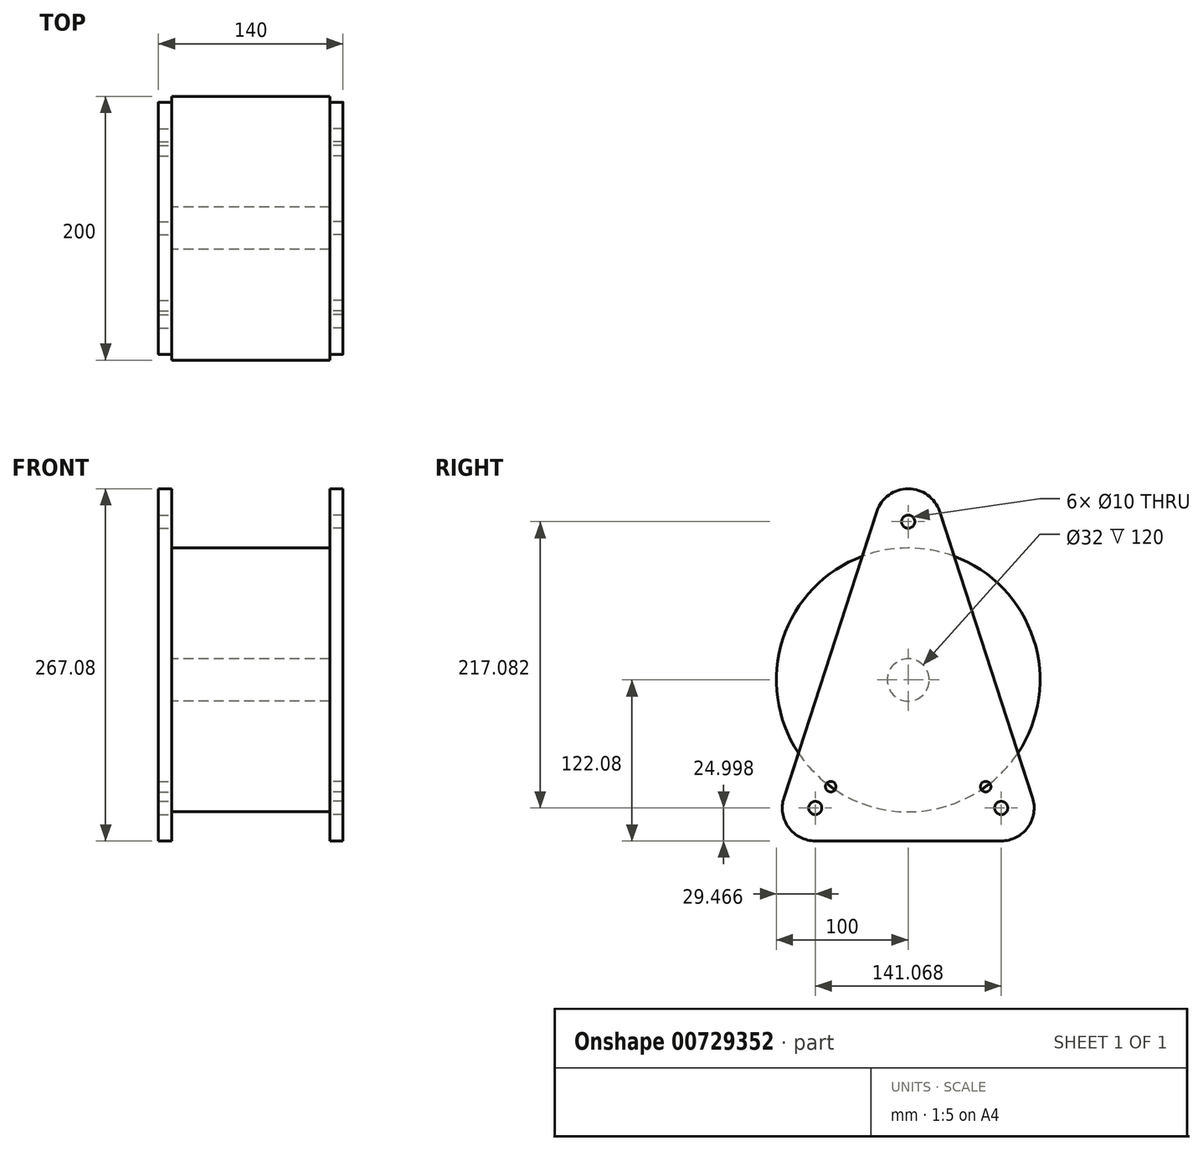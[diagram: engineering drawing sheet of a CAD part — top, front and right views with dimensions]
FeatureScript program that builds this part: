
annotation { "Feature Type Name" : "Feature", "Feature Type Description" : "" }
export const myFeature = defineFeature(function(context is Context, id is Id, definition is map)
    precondition{}
    {
        {
            var Q0;
            Q0=qCreatedBy(makeId("Right.planeOp"),FACE);
            var sketch = newSketch(context, id + "F0", { "sketchPlane" : qUnion([Q0])});
            skCircle(sketch, "E0", {"center": v(0, 0) * mm, "radius": 100 * mm});
            skCircle(sketch, "E1", {"center": v(0, 0) * mm, "radius": 16 * mm});
            skSolve(sketch);
        }
        {
            var Q0;
            Q0=makeQuery(id+"F0.imprint","IMPRINT",FACE,{"disambiguationData":[TD([[makeQuery(id+"F0.imprint","IMPRINT",EDGE,{"derivedFrom":sQuery(id+"F0.wireOp",EDGE,"E0")}),1.0]])]});
            extrude(context, id + "F1", {"entities" : qUnion([Q0]), "depth" : 60 * mm, "offsetDistance" : 25 * mm});
        }
        {
            var Q0;
            Q0=makeQuery(id+"F1.opExtrude","CAP_FACE",FACE,{"disambiguationData":[OSD([sQuery(id+"F0.wireOp",EDGE,"E0"),sQuery(id+"F0.wireOp",EDGE,"E1")])],"isStart":false});
            var sketch = newSketch(context, id + "F2", { "sketchPlane" : qUnion([Q0])});
            skLineSegment(sketch, "E2", {"start": v(0, 0) * mm, "end": v(0, 120) * mm, "construction": true});
            skLineSegment(sketch, "E3.2.0", {"start": v(0, 0) * mm, "end": v(-70.53, -97.08) * mm, "construction": true});
            skLineSegment(sketch, "E3.3.0", {"start": v(0, 0) * mm, "end": v(70.53, -97.08) * mm, "construction": true});
            skPoint(sketch, "E3.center", {"position": v(0, 0) * mm});
            skArc(sketch, "E4", {"start": v(-94.31, -89.36) * mm, "mid": v(-90.76, -111.78) * mm, "end": v(-70.53, -122.08) * mm});
            skArc(sketch, "E5", {"start": v(70.53, -122.08) * mm, "mid": v(90.76, -111.78) * mm, "end": v(94.31, -89.36) * mm});
            skLineSegment(sketch, "E6", {"start": v(0, 120) * mm, "end": v(-70.53, -97.08) * mm, "construction": true});
            skLineSegment(sketch, "E7", {"start": v(70.53, -97.08) * mm, "end": v(0, 120) * mm, "construction": true});
            skLineSegment(sketch, "E8", {"start": v(70.53, -97.08) * mm, "end": v(-70.53, -97.08) * mm, "construction": true});
            skLineSegment(sketch, "E9", {"start": v(-23.78, 127.73) * mm, "end": v(-94.31, -89.36) * mm});
            skLineSegment(sketch, "E10", {"start": v(23.78, 127.73) * mm, "end": v(94.31, -89.36) * mm});
            skLineSegment(sketch, "E11", {"start": v(-70.53, -122.08) * mm, "end": v(70.53, -122.08) * mm});
            skPoint(sketch, "E12", {"position": v(-94.31, -89.36) * mm});
            skPoint(sketch, "E13", {"position": v(-70.53, -122.08) * mm});
            skPoint(sketch, "E14", {"position": v(70.53, -122.08) * mm});
            skPoint(sketch, "E15", {"position": v(94.31, -89.36) * mm});
            skPoint(sketch, "E16", {"position": v(23.78, 127.73) * mm});
            skPoint(sketch, "E17", {"position": v(-23.78, 127.73) * mm});
            skArc(sketch, "E18.trimOffspring", {"start": v(23.78, 127.73) * mm, "mid": v(0, 145) * mm, "end": v(-23.78, 127.73) * mm});
            skPoint(sketch, "E19", {"position": v(-58.78, -80.9) * mm});
            skPoint(sketch, "E20", {"position": v(58.78, -80.9) * mm});
            skCircle(sketch, "E21", {"center": v(-58.78, -80.9) * mm, "radius": 4 * mm});
            skCircle(sketch, "E22", {"center": v(58.78, -80.9) * mm, "radius": 4 * mm});
            skCircle(sketch, "E23", {"center": v(-70.53, -97.08) * mm, "radius": 5 * mm});
            skCircle(sketch, "E24", {"center": v(70.53, -97.08) * mm, "radius": 5 * mm});
            skCircle(sketch, "E25", {"center": v(0, 120) * mm, "radius": 5 * mm});
            skSolve(sketch);
        }
        {
            var Q0;
            {var subQ9=sQuery(id+"F2.wireOp",EDGE,"E4");Q0=makeQuery(id+"F2.imprint","IMPRINT",FACE,{"disambiguationData":[TD([[makeQuery(id+"F2.imprint","IMPRINT",EDGE,{"derivedFrom":subQ9}),1.0]])]});}
            var Q1;
            Q1=makeQuery(id+"F2.imprint","IMPRINT",FACE,{"disambiguationData":[TD([[makeQuery(id+"F2.imprint","IMPRINT",EDGE,{"derivedFrom":makeQuery(id+"F1.opExtrude","CAP_EDGE",EDGE,{"disambiguationData":[OSD([sQuery(id+"F0.wireOp",EDGE,"E1")])],"isStart":false})}),-1.0]])]});
            var Q2;
            {var subQ0=sQuery(id+"F2.wireOp",EDGE,"E18.trimOffspring");Q2=makeQuery(id+"F2.imprint","IMPRINT",FACE,{"disambiguationData":[TD([[makeQuery(id+"F2.imprint","IMPRINT",EDGE,{"derivedFrom":subQ0}),1.0]])]});}
            var Q3;
            Q3=makeQuery(id+"F2.imprint","IMPRINT",FACE,{"disambiguationData":[TD([[makeQuery(id+"F2.imprint","IMPRINT",EDGE,{"derivedFrom":makeQuery(id+"F1.opExtrude","CAP_EDGE",EDGE,{"disambiguationData":[OSD([sQuery(id+"F0.wireOp",EDGE,"E1")])],"isStart":false})}),1.0]])]});
            extrude(context, id + "F3", {"entities" : qUnion([Q0, Q1, Q2, Q3]), "operationType" : NewBodyOperationType.ADD, "depth" : 10 * mm, "offsetDistance" : 25 * mm});
        }
        {
            var Q0;
            Q0=makeQuery(id+"F1.opExtrude","SWEPT_BODY",BODY,{"disambiguationData":[OSD([sQuery(id+"F0.wireOp",EDGE,"E0"),sQuery(id+"F0.wireOp",EDGE,"E1")])]});
            var Q1;
            Q1=makeQuery(id+"F1.opExtrude","CAP_FACE",FACE,{"disambiguationData":[OSD([sQuery(id+"F0.wireOp",EDGE,"E0"),sQuery(id+"F0.wireOp",EDGE,"E1")])],"isStart":true});
            mirror(context, id + "F4", {"operationType" : NewBodyOperationType.ADD, "entities" : qUnion([Q0]), "mirrorPlane" : qUnion([Q1])});
        }
    });
